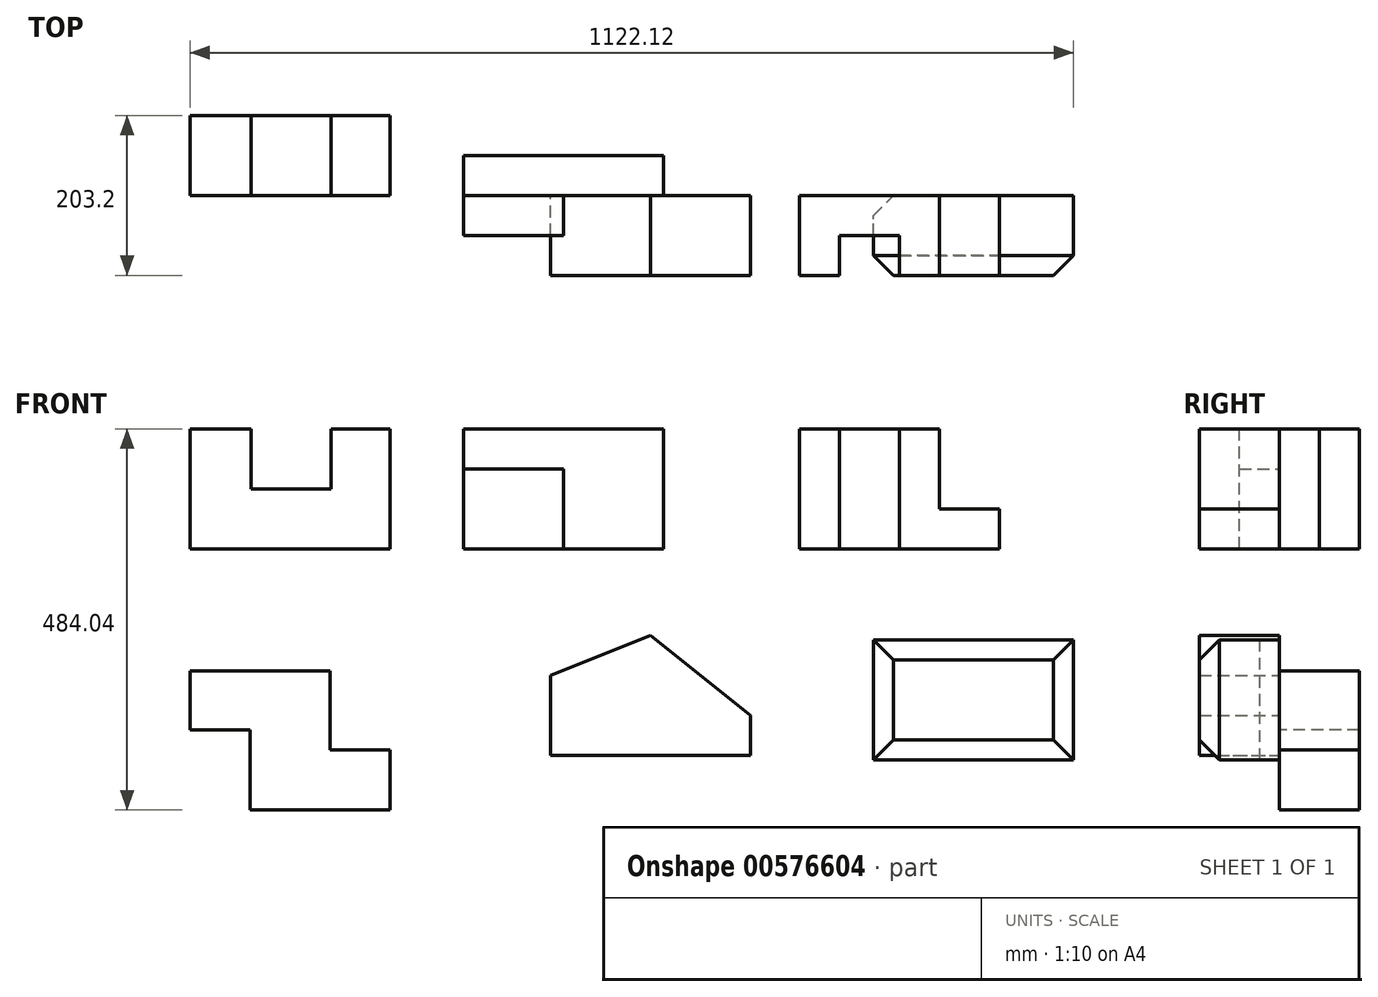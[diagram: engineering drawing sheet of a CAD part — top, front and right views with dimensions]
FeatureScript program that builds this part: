
annotation { "Feature Type Name" : "Feature", "Feature Type Description" : "" }
export const myFeature = defineFeature(function(context is Context, id is Id, definition is map)
    precondition{}
    {
        {
            var Q0;
            Q0=qCreatedBy(makeId("Front.planeOp"),FACE);
            var sketch = newSketch(context, id + "F0", { "sketchPlane" : qUnion([Q0])});
            skLineSegment(sketch, "E0", {"start": v(0, 0) * mm, "end": v(0, 152.4) * mm});
            skLineSegment(sketch, "E1", {"start": v(0, 152.4) * mm, "end": v(77.46, 152.4) * mm});
            skLineSegment(sketch, "E2", {"start": v(77.46, 152.4) * mm, "end": v(77.46, 76.2) * mm});
            skLineSegment(sketch, "E3", {"start": v(77.46, 76.2) * mm, "end": v(179.06, 76.2) * mm});
            skLineSegment(sketch, "E4", {"start": v(179.06, 76.2) * mm, "end": v(179.06, 152.4) * mm});
            skLineSegment(sketch, "E5", {"start": v(179.06, 152.4) * mm, "end": v(254, 152.4) * mm});
            skLineSegment(sketch, "E6", {"start": v(254, 152.4) * mm, "end": v(254, 0) * mm});
            skLineSegment(sketch, "E7", {"start": v(254, 0) * mm, "end": v(0, 0) * mm});
            skSolve(sketch);
        }
        {
            var Q0;
            Q0=makeQuery(id+"F0.imprint","IMPRINT",FACE,{"disambiguationData":[TD([[makeQuery(id+"F0.imprint","IMPRINT",EDGE,{"derivedFrom":sQuery(id+"F0.wireOp",EDGE,"E0")}),-1.0]])]});
            extrude(context, id + "F1", {"entities" : qUnion([Q0]), "oppositeDirection" : true, "depth" : 101.6 * mm, "offsetDistance" : 25.4 * mm});
        }
        {
            var Q0;
            Q0=qCreatedBy(makeId("Front.planeOp"),FACE);
            var sketch = newSketch(context, id + "F2", { "sketchPlane" : qUnion([Q0])});
            skLineSegment(sketch, "E8", {"start": v(347.19, 0) * mm, "end": v(347.19, 152.4) * mm});
            skLineSegment(sketch, "E9", {"start": v(347.19, 152.4) * mm, "end": v(601.19, 152.4) * mm});
            skLineSegment(sketch, "E10", {"start": v(601.19, 152.4) * mm, "end": v(601.19, 0) * mm});
            skLineSegment(sketch, "E11", {"start": v(601.19, 0) * mm, "end": v(347.19, 0) * mm});
            skSolve(sketch);
        }
        {
            var Q0;
            Q0=makeQuery(id+"F2.imprint","IMPRINT",FACE,{"disambiguationData":[TD([[makeQuery(id+"F2.imprint","IMPRINT",EDGE,{"derivedFrom":sQuery(id+"F2.wireOp",EDGE,"E8")}),-1.0]])]});
            extrude(context, id + "F3", {"entities" : qUnion([Q0]), "oppositeDirection" : true, "depth" : 50.8 * mm, "offsetDistance" : 25.4 * mm});
        }
        {
            var Q0;
            Q0=makeQuery(id+"F3.opExtrude","CAP_FACE",FACE,{"disambiguationData":[OSD([sQuery(id+"F2.wireOp",EDGE,"E8"),sQuery(id+"F2.wireOp",EDGE,"E9"),sQuery(id+"F2.wireOp",EDGE,"E10"),sQuery(id+"F2.wireOp",EDGE,"E11")])],"isStart":true});
            var sketch = newSketch(context, id + "F4", { "sketchPlane" : qUnion([Q0])});
            skLineSegment(sketch, "E12.bottom", {"start": v(347.19, 0) * mm, "end": v(474.19, 0) * mm});
            skLineSegment(sketch, "E12.top", {"start": v(347.19, 101.6) * mm, "end": v(474.19, 101.6) * mm});
            skLineSegment(sketch, "E12.left", {"start": v(347.19, 0) * mm, "end": v(347.19, 101.6) * mm});
            skLineSegment(sketch, "E12.right", {"start": v(474.19, 0) * mm, "end": v(474.19, 101.6) * mm});
            skSolve(sketch);
        }
        {
            var Q0;
            Q0=makeQuery(id+"F4.imprint","IMPRINT",FACE,{"disambiguationData":[TD([[makeQuery(id+"F4.imprint","IMPRINT",EDGE,{"derivedFrom":sQuery(id+"F4.wireOp",EDGE,"E12.bottom")}),-1.0]])]});
            extrude(context, id + "F5", {"entities" : qUnion([Q0]), "operationType" : NewBodyOperationType.ADD, "depth" : 50.8 * mm, "offsetDistance" : 25.4 * mm});
        }
        {
            var Q0;
            Q0=qCreatedBy(makeId("Front.planeOp"),FACE);
            var sketch = newSketch(context, id + "F6", { "sketchPlane" : qUnion([Q0])});
            skLineSegment(sketch, "E13", {"start": v(774.3, 0) * mm, "end": v(774.3, 152.4) * mm});
            skLineSegment(sketch, "E14", {"start": v(774.3, 152.4) * mm, "end": v(952.1, 152.4) * mm});
            skLineSegment(sketch, "E15", {"start": v(952.1, 152.4) * mm, "end": v(952.1, 50.8) * mm});
            skLineSegment(sketch, "E16", {"start": v(952.1, 50.8) * mm, "end": v(1028.3, 50.8) * mm});
            skLineSegment(sketch, "E17", {"start": v(1028.3, 50.8) * mm, "end": v(1028.3, 0) * mm});
            skLineSegment(sketch, "E18", {"start": v(1028.3, 0) * mm, "end": v(774.3, 0) * mm});
            skSolve(sketch);
        }
        {
            var Q0;
            Q0=makeQuery(id+"F6.imprint","IMPRINT",FACE,{"disambiguationData":[TD([[makeQuery(id+"F6.imprint","IMPRINT",EDGE,{"derivedFrom":sQuery(id+"F6.wireOp",EDGE,"E13")}),-1.0]])]});
            extrude(context, id + "F7", {"entities" : qUnion([Q0]), "depth" : 101.6 * mm, "offsetDistance" : 25.4 * mm});
        }
        {
            var Q0;
            Q0=makeQuery(id+"F7.opExtrude","SWEPT_FACE",FACE,{"disambiguationData":[OSD([sQuery(id+"F6.wireOp",EDGE,"E14")])]});
            var sketch = newSketch(context, id + "F8", { "sketchPlane" : qUnion([Q0])});
            skLineSegment(sketch, "E19", {"start": v(825.1, -101.6) * mm, "end": v(825.1, -50.8) * mm});
            skLineSegment(sketch, "E20", {"start": v(825.1, -50.8) * mm, "end": v(901.3, -50.8) * mm});
            skLineSegment(sketch, "E21", {"start": v(901.3, -50.8) * mm, "end": v(901.3, -101.6) * mm});
            skSolve(sketch);
        }
        {
            var Q0;
            {var subQ0=sQuery(id+"F8.wireOp",EDGE,"E19");Q0=makeQuery(id+"F8.imprint","IMPRINT",FACE,{"disambiguationData":[TD([[makeQuery(id+"F8.imprint","IMPRINT",EDGE,{"derivedFrom":subQ0}),-1.0]])]});}
            extrude(context, id + "F9", {"entities" : qUnion([Q0]), "operationType" : NewBodyOperationType.REMOVE, "oppositeDirection" : true, "depth" : 152.4 * mm, "offsetDistance" : 25.4 * mm});
        }
        {
            var Q0;
            Q0=qCreatedBy(makeId("Front.planeOp"),FACE);
            var sketch = newSketch(context, id + "F10", { "sketchPlane" : qUnion([Q0])});
            skLineSegment(sketch, "E22", {"start": v(0, -155.04) * mm, "end": v(177.8, -155.04) * mm});
            skLineSegment(sketch, "E23", {"start": v(177.8, -155.04) * mm, "end": v(177.8, -255.44) * mm});
            skLineSegment(sketch, "E24", {"start": v(177.8, -255.44) * mm, "end": v(254, -255.44) * mm});
            skLineSegment(sketch, "E25", {"start": v(254, -255.44) * mm, "end": v(254, -331.64) * mm});
            skLineSegment(sketch, "E26", {"start": v(254, -331.64) * mm, "end": v(76.2, -331.64) * mm});
            skLineSegment(sketch, "E27", {"start": v(76.2, -331.64) * mm, "end": v(76.2, -230.04) * mm});
            skLineSegment(sketch, "E28", {"start": v(76.2, -230.04) * mm, "end": v(0, -230.04) * mm});
            skLineSegment(sketch, "E29", {"start": v(0, -230.04) * mm, "end": v(0, -155.04) * mm});
            skSolve(sketch);
        }
        {
            var Q0;
            Q0=makeQuery(id+"F10.imprint","IMPRINT",FACE,{"disambiguationData":[TD([[makeQuery(id+"F10.imprint","IMPRINT",EDGE,{"derivedFrom":sQuery(id+"F10.wireOp",EDGE,"E22")}),-1.0]])]});
            extrude(context, id + "F11", {"entities" : qUnion([Q0]), "oppositeDirection" : true, "depth" : 101.6 * mm, "offsetDistance" : 25.4 * mm});
        }
        {
            var Q0;
            Q0=qCreatedBy(makeId("Front.planeOp"),FACE);
            var sketch = newSketch(context, id + "F12", { "sketchPlane" : qUnion([Q0])});
            skLineSegment(sketch, "E30", {"start": v(458.07, -160.63) * mm, "end": v(458.07, -262.23) * mm});
            skLineSegment(sketch, "E31", {"start": v(458.07, -262.23) * mm, "end": v(712.07, -262.23) * mm});
            skLineSegment(sketch, "E32", {"start": v(712.07, -262.23) * mm, "end": v(712.07, -211.43) * mm});
            skLineSegment(sketch, "E33", {"start": v(712.07, -211.43) * mm, "end": v(585.07, -109.83) * mm});
            skLineSegment(sketch, "E34", {"start": v(585.07, -109.83) * mm, "end": v(458.07, -160.63) * mm});
            skSolve(sketch);
        }
        {
            var Q0;
            Q0 = qSketchRegion(id + "F12", true);
            extrude(context, id + "F13", {"entities" : qUnion([Q0]), "depth" : 101.6 * mm, "offsetDistance" : 25.4 * mm});
        }
        {
            var Q0;
            Q0=qCreatedBy(makeId("Front.planeOp"),FACE);
            var sketch = newSketch(context, id + "F14", { "sketchPlane" : qUnion([Q0])});
            skLineSegment(sketch, "E35", {"start": v(868.12, -115.35) * mm, "end": v(868.12, -267.75) * mm});
            skLineSegment(sketch, "E36", {"start": v(1122.12, -267.75) * mm, "end": v(1122.12, -115.35) * mm});
            skLineSegment(sketch, "E37", {"start": v(1122.12, -115.35) * mm, "end": v(868.12, -115.35) * mm});
            skPoint(sketch, "E38.orphan", {"position": v(868.12, -104.82) * mm});
            skLineSegment(sketch, "E39", {"start": v(868.12, -267.75) * mm, "end": v(1122.12, -267.75) * mm});
            skSolve(sketch);
        }
        {
            var Q0;
            Q0 = qSketchRegion(id + "F14", true);
            extrude(context, id + "F15", {"entities" : qUnion([Q0]), "depth" : 101.6 * mm, "offsetDistance" : 25.4 * mm});
        }
        {
            var Q0;
            Q0=makeQuery(id+"F15.opExtrude","CAP_EDGE",EDGE,{"disambiguationData":[OSD([sQuery(id+"F14.wireOp",EDGE,"E35")])],"isStart":true});
            var Q1;
            Q1=makeQuery(id+"F15.opExtrude","CAP_EDGE",EDGE,{"disambiguationData":[OSD([sQuery(id+"F14.wireOp",EDGE,"E37")])],"isStart":false});
            var Q2;
            Q2=makeQuery(id+"F15.opExtrude","CAP_EDGE",EDGE,{"disambiguationData":[OSD([sQuery(id+"F14.wireOp",EDGE,"E36")])],"isStart":false});
            var Q3;
            Q3=makeQuery(id+"F15.opExtrude","CAP_EDGE",EDGE,{"disambiguationData":[OSD([sQuery(id+"F14.wireOp",EDGE,"E39")])],"isStart":false});
            var Q4;
            Q4=makeQuery(id+"F15.opExtrude","CAP_EDGE",EDGE,{"disambiguationData":[OSD([sQuery(id+"F14.wireOp",EDGE,"E35")])],"isStart":false});
            chamfer(context, id + "F16", {"entities" : qUnion([Q0, Q1, Q2, Q3, Q4]), "width" : 25.4 * mm, "tangentPropagation" : true});
        }
    });
